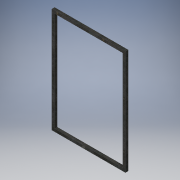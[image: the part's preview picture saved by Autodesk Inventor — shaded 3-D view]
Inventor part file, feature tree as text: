
AUTODESK INVENTOR PART (.ipt)
format: ipt  version: 2019 (Build 230136000, 136)  size: 108,544 bytes
history: native  units: mm
features: extrude x1, sketch x1
ambient origin geometry x8: Origin, YZ Plane, XZ Plane, XY Plane, X Axis, Y Axis, Z Axis, Center Point
bodies: Solid1 (feature_tree)
feature tree (2):
  extrude  "Extrusion1"  Depth=400.0mm
  sketch  "Sketch1"  dims[d0=280.0mm d1=400.0mm d2=10.0mm d3=10.0mm d4=10.0mm d5=10.0mm d6=150.769231mm d7=249.230769mm d8=10.0mm d9=0.0mm]
